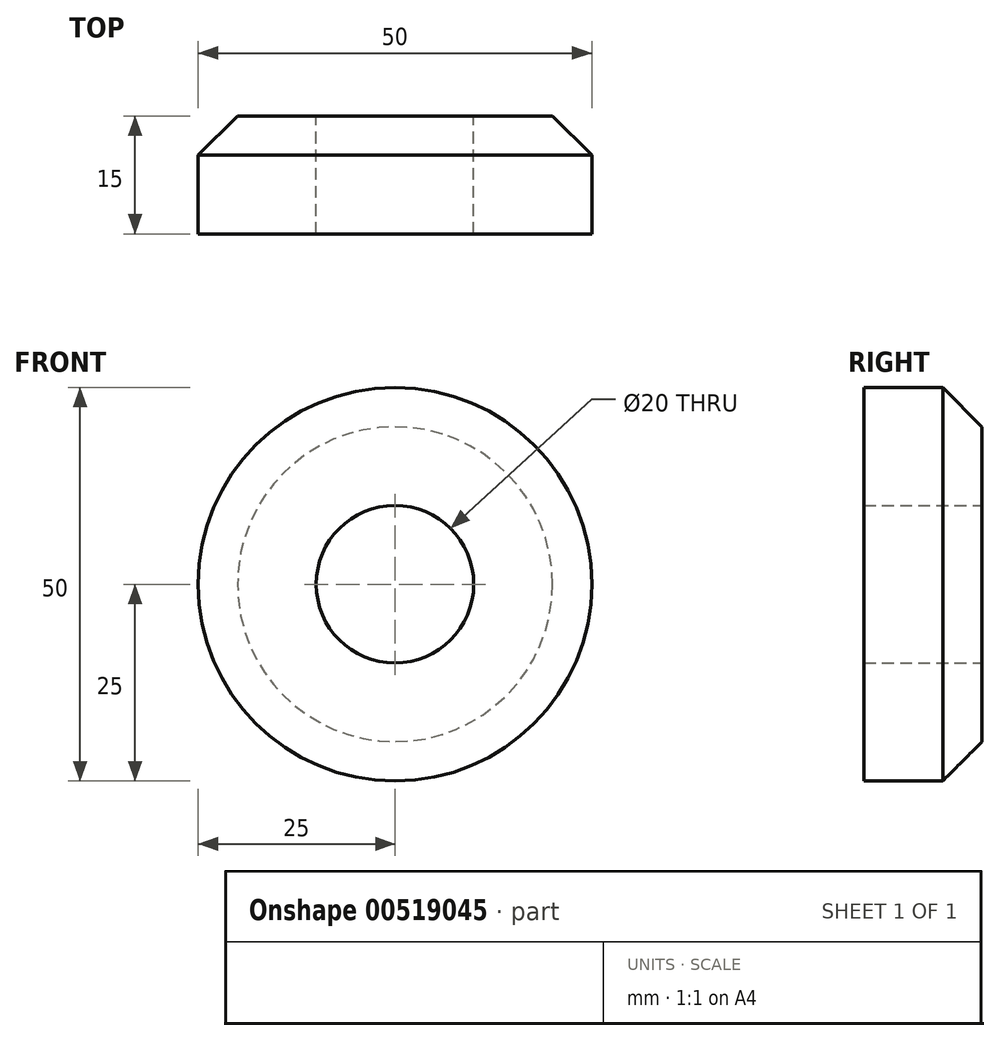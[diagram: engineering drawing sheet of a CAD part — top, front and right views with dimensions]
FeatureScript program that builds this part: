
annotation { "Feature Type Name" : "Feature", "Feature Type Description" : "" }
export const myFeature = defineFeature(function(context is Context, id is Id, definition is map)
    precondition{}
    {
        {
            var Q0;
            Q0=qCreatedBy(makeId("Front.planeOp"),FACE);
            var sketch = newSketch(context, id + "F0", { "sketchPlane" : qUnion([Q0])});
            skCircle(sketch, "E0", {"center": v(0, 0) * mm, "radius": 10 * mm});
            skCircle(sketch, "E1", {"center": v(0, 0) * mm, "radius": 25 * mm});
            skSolve(sketch);
        }
        {
            var Q0;
            Q0 = qSketchRegion(id + "F0", true);
            extrude(context, id + "F1", {"entities" : qUnion([Q0]), "depth" : 15 * mm, "offsetDistance" : 25 * mm});
        }
        {
            var Q0;
            Q0=makeQuery(id+"F1.opExtrude","CAP_EDGE",EDGE,{"disambiguationData":[OSD([sQuery(id+"F0.wireOp",EDGE,"E1")])],"isStart":true});
            chamfer(context, id + "F2", {"entities" : qUnion([Q0]), "width" : 5 * mm, "tangentPropagation" : true});
        }
    });
